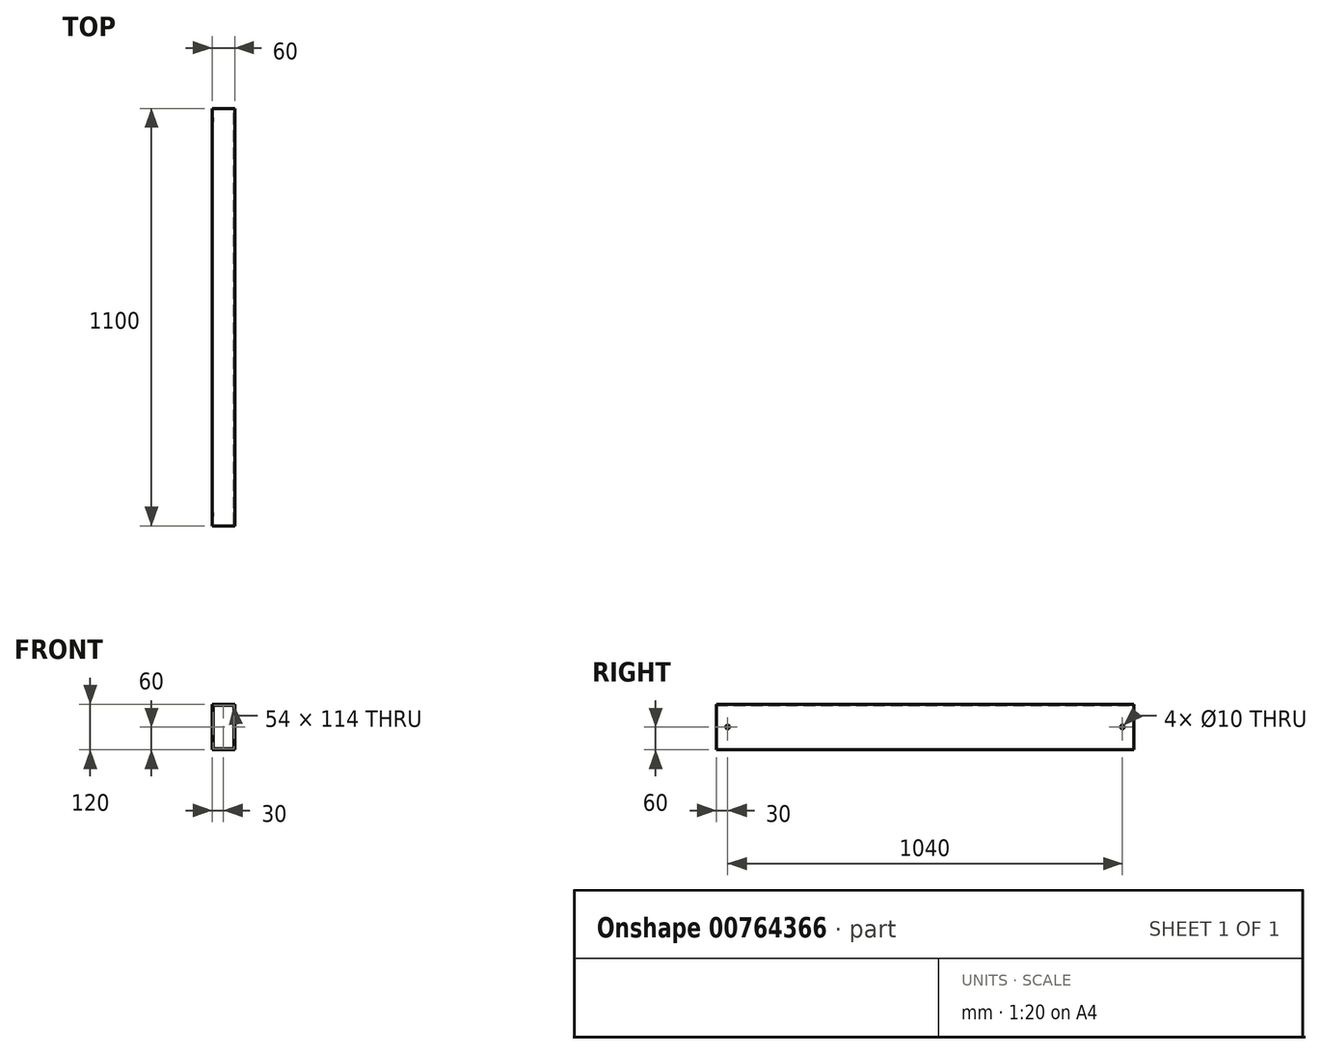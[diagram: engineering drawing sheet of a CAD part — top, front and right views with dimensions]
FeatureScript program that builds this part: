
annotation { "Feature Type Name" : "Feature", "Feature Type Description" : "" }
export const myFeature = defineFeature(function(context is Context, id is Id, definition is map)
    precondition{}
    {
        {
            var Q0;
            Q0=qCreatedBy(makeId("Front.planeOp"),FACE);
            var sketch = newSketch(context, id + "F0", { "sketchPlane" : qUnion([Q0])});
            skLineSegment(sketch, "E0", {"start": v(-30, 0) * mm, "end": v(-30, 60) * mm});
            skLineSegment(sketch, "E1", {"start": v(-30, 60) * mm, "end": v(30, 60) * mm});
            skLineSegment(sketch, "E2", {"start": v(30, 60) * mm, "end": v(30, -60) * mm});
            skLineSegment(sketch, "E3", {"start": v(30, -60) * mm, "end": v(-30, -60) * mm});
            skLineSegment(sketch, "E4", {"start": v(-30, -60) * mm, "end": v(-30, 0) * mm});
            skLineSegment(sketch, "E5.0", {"start": v(-27, 57) * mm, "end": v(27, 57) * mm});
            skLineSegment(sketch, "E5.1", {"start": v(-27, 0) * mm, "end": v(-27, 57) * mm});
            skLineSegment(sketch, "E5.2", {"start": v(27, 57) * mm, "end": v(27, -57) * mm});
            skLineSegment(sketch, "E5.3", {"start": v(27, -57) * mm, "end": v(-27, -57) * mm});
            skLineSegment(sketch, "E5.4", {"start": v(-27, -57) * mm, "end": v(-27, 0) * mm});
            skSolve(sketch);
        }
        {
            var Q0;
            Q0=makeQuery(id+"F0.imprint","IMPRINT",FACE,{"disambiguationData":[TD([[makeQuery(id+"F0.imprint","IMPRINT",EDGE,{"derivedFrom":sQuery(id+"F0.wireOp",EDGE,"E0")}),-1.0]])]});
            extrude(context, id + "F1", {"entities" : qUnion([Q0]), "depth" : 1100 * mm, "offsetDistance" : 25 * mm, "symmetric" : true});
        }
        {
            var Q0;
            Q0=makeQuery(id+"F1.opExtrude","SWEPT_FACE",FACE,{"disambiguationData":[OSD([sQuery(id+"F0.wireOp",EDGE,"E2")])]});
            var sketch = newSketch(context, id + "F2", { "sketchPlane" : qUnion([Q0])});
            skCircle(sketch, "E6", {"center": v(520, 0) * mm, "radius": 5 * mm});
            skPoint(sketch, "E6.centerSnap0", {"position": v(550, 0) * mm});
            skCircle(sketch, "E7", {"center": v(-520, 0) * mm, "radius": 5 * mm});
            skPoint(sketch, "E7.centerSnap0", {"position": v(-550, 0) * mm});
            skSolve(sketch);
        }
        {
            var Q0;
            Q0=sQuery(id+"F2.wireOp",VERTEX,"E6.center");
            var Q1;
            Q1=sQuery(id+"F2.wireOp",VERTEX,"E7.center");
            var Q2;
            Q2=makeQuery(id+"F1.opExtrude","SWEPT_BODY",BODY,{"disambiguationData":[OSD([sQuery(id+"F0.wireOp",EDGE,"E0"),sQuery(id+"F0.wireOp",EDGE,"E1"),sQuery(id+"F0.wireOp",EDGE,"E2"),sQuery(id+"F0.wireOp",EDGE,"E3"),sQuery(id+"F0.wireOp",EDGE,"E4"),sQuery(id+"F0.wireOp",EDGE,"E5.0"),sQuery(id+"F0.wireOp",EDGE,"E5.1"),sQuery(id+"F0.wireOp",EDGE,"E5.2"),sQuery(id+"F0.wireOp",EDGE,"E5.3"),sQuery(id+"F0.wireOp",EDGE,"E5.4")])]});
            hole(context, id + "F3", {"style" : HoleStyle.SIMPLE, "endStyle" : HoleEndStyle.THROUGH, "holeDiameter" : 10 * mm, "majorDiameter" : 5 * mm, "isTappedThrough" : true, "tappedDepth" : 12 * mm, "tapClearance" : 3, "locations" : qUnion([Q0, Q1]), "scope" : qUnion([Q2]), "startStyle" : HoleStartStyle.PART});
        }
    });
